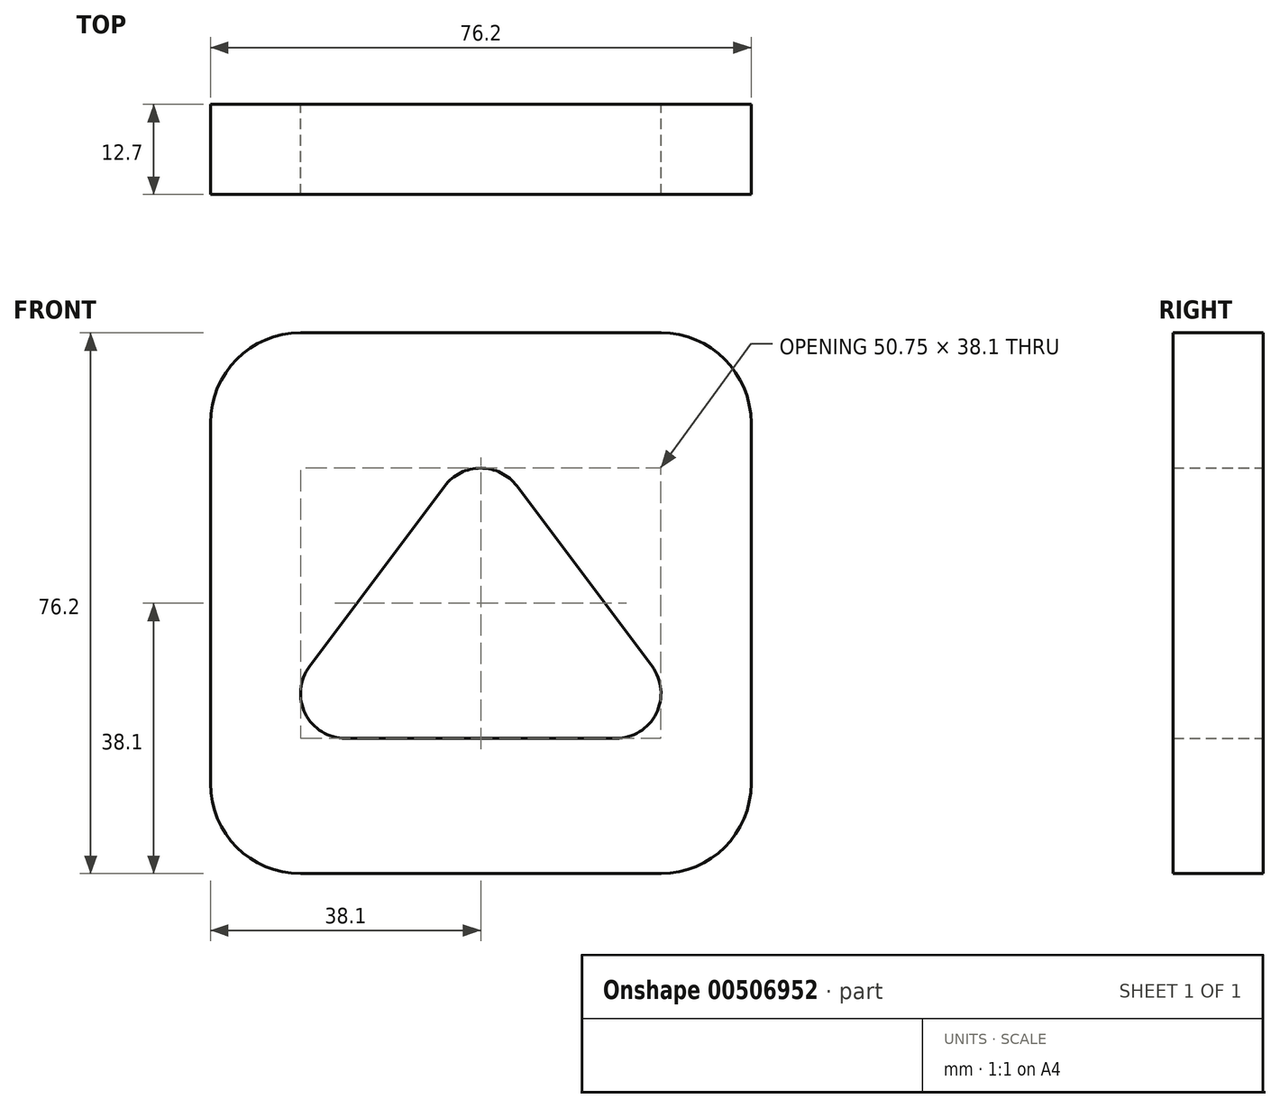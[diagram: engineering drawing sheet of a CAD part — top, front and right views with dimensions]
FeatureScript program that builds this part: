
annotation { "Feature Type Name" : "Feature", "Feature Type Description" : "" }
export const myFeature = defineFeature(function(context is Context, id is Id, definition is map)
    precondition{}
    {
        {
            var Q0;
            Q0=qCreatedBy(makeId("Front.planeOp"),FACE);
            var sketch = newSketch(context, id + "F0", { "sketchPlane" : qUnion([Q0])});
            skLineSegment(sketch, "E0", {"start": v(12.7, 0) * mm, "end": v(63.5, 0) * mm});
            skLineSegment(sketch, "E1", {"start": v(76.2, 12.7) * mm, "end": v(76.2, 63.5) * mm});
            skLineSegment(sketch, "E2", {"start": v(63.5, 76.2) * mm, "end": v(12.7, 76.2) * mm});
            skLineSegment(sketch, "E3", {"start": v(0, 63.5) * mm, "end": v(0, 12.7) * mm});
            skArc(sketch, "E4", {"start": v(13.97, 29.21) * mm, "mid": v(13.37, 22.56) * mm, "end": v(19.05, 19.05) * mm});
            skArc(sketch, "E5", {"start": v(57.15, 19.05) * mm, "mid": v(62.83, 22.56) * mm, "end": v(62.23, 29.21) * mm});
            skArc(sketch, "E6", {"start": v(43.18, 54.6) * mm, "mid": v(38.1, 57.15) * mm, "end": v(33.02, 54.6) * mm});
            skLineSegment(sketch, "E7", {"start": v(33.02, 54.6) * mm, "end": v(13.97, 29.21) * mm});
            skLineSegment(sketch, "E8", {"start": v(43.18, 54.6) * mm, "end": v(62.23, 29.21) * mm});
            skLineSegment(sketch, "E9", {"start": v(19.05, 19.05) * mm, "end": v(57.15, 19.05) * mm});
            skArc(sketch, "E10", {"start": v(12.7, 76.2) * mm, "mid": v(3.72, 72.48) * mm, "end": v(0, 63.5) * mm});
            skPoint(sketch, "E11.orphan", {"position": v(0, 76.2) * mm});
            skArc(sketch, "E12", {"start": v(76.2, 63.5) * mm, "mid": v(72.48, 72.48) * mm, "end": v(63.5, 76.2) * mm});
            skArc(sketch, "E13", {"start": v(0, 12.7) * mm, "mid": v(3.72, 3.72) * mm, "end": v(12.7, 0) * mm});
            skArc(sketch, "E14", {"start": v(63.5, 0) * mm, "mid": v(72.48, 3.72) * mm, "end": v(76.2, 12.7) * mm});
            skSolve(sketch);
        }
        {
            var Q0;
            Q0=makeQuery(id+"F0.imprint","IMPRINT",FACE,{"disambiguationData":[TD([[makeQuery(id+"F0.imprint","IMPRINT",EDGE,{"derivedFrom":sQuery(id+"F0.wireOp",EDGE,"E0")}),1.0]])]});
            extrude(context, id + "F1", {"entities" : qUnion([Q0]), "depth" : 12.7 * mm});
        }
    });
